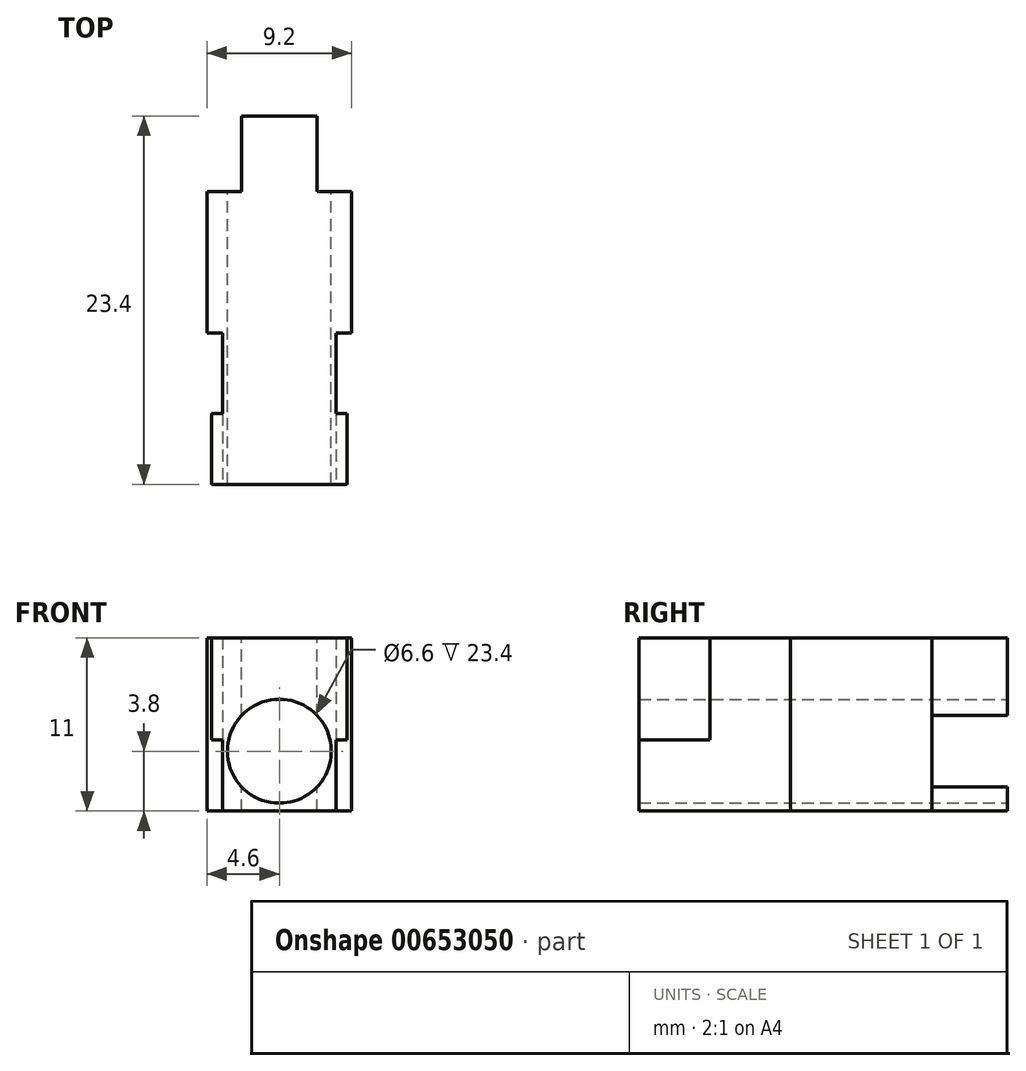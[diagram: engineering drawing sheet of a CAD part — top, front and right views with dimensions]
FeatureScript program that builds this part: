
annotation { "Feature Type Name" : "Feature", "Feature Type Description" : "" }
export const myFeature = defineFeature(function(context is Context, id is Id, definition is map)
    precondition{}
    {
        {
            var Q0;
            Q0=qCreatedBy(makeId("Front.planeOp"),FACE);
            var sketch = newSketch(context, id + "F0", { "sketchPlane" : qUnion([Q0])});
            skLineSegment(sketch, "E0.bottom", {"start": v(-3.6, 5.5) * mm, "end": v(3.6, 5.5) * mm});
            skLineSegment(sketch, "E0.top", {"start": v(-3.6, -5.5) * mm, "end": v(3.6, -5.5) * mm});
            skLineSegment(sketch, "E0.left", {"start": v(-3.6, 5.5) * mm, "end": v(-3.6, -5.5) * mm});
            skLineSegment(sketch, "E0.right", {"start": v(3.6, 5.5) * mm, "end": v(3.6, -5.5) * mm});
            skPoint(sketch, "E0.middle", {"position": v(0, 0) * mm});
            skCircle(sketch, "E1", {"center": v(0, -1.7) * mm, "radius": 3.3 * mm});
            skSolve(sketch);
        }
        {
            var Q0;
            Q0 = qSketchRegion(id + "F0", true);
            extrude(context, id + "F1", {"entities" : qUnion([Q0]), "depth" : 23.4 * mm, "offsetDistance" : 25 * mm});
        }
        {
            var Q0;
            Q0=makeQuery(id+"F1.opExtrude","SWEPT_FACE",FACE,{"disambiguationData":[OSD([sQuery(id+"F0.wireOp",EDGE,"E0.bottom")])]});
            var sketch = newSketch(context, id + "F2", { "sketchPlane" : qUnion([Q0])});
            skLineSegment(sketch, "E2.right", {"start": v(2.4, 0) * mm, "end": v(2.4, -4.8) * mm});
            skLineSegment(sketch, "E3.bottom", {"start": v(2.4, 0) * mm, "end": v(3.6, 0) * mm});
            skLineSegment(sketch, "E3.top", {"start": v(2.4, -4.8) * mm, "end": v(3.6, -4.8) * mm});
            skLineSegment(sketch, "E3.right", {"start": v(3.6, 0) * mm, "end": v(3.6, -4.8) * mm});
            skLineSegment(sketch, "E4.bottom", {"start": v(-2.4, 0) * mm, "end": v(-3.6, 0) * mm});
            skLineSegment(sketch, "E4.top", {"start": v(-2.4, -4.8) * mm, "end": v(-3.6, -4.8) * mm});
            skLineSegment(sketch, "E4.left", {"start": v(-2.4, 0) * mm, "end": v(-2.4, -4.8) * mm});
            skLineSegment(sketch, "E4.right", {"start": v(-3.6, 0) * mm, "end": v(-3.6, -4.8) * mm});
            skSolve(sketch);
        }
        {
            var Q0;
            Q0 = qSketchRegion(id + "F2", true);
            extrude(context, id + "F3", {"entities" : qUnion([Q0]), "operationType" : NewBodyOperationType.REMOVE, "endBound" : BoundingType.THROUGH_ALL, "oppositeDirection" : true, "depth" : 25 * mm, "offsetDistance" : 25 * mm});
        }
        {
            var Q0;
            Q0=makeQuery(id+"F1.opExtrude","SWEPT_FACE",FACE,{"disambiguationData":[OSD([sQuery(id+"F0.wireOp",EDGE,"E0.bottom")])]});
            var sketch = newSketch(context, id + "F4", { "sketchPlane" : qUnion([Q0])});
            skLineSegment(sketch, "E5.bottom", {"start": v(-4.6, -4.8) * mm, "end": v(4.6, -4.8) * mm});
            skLineSegment(sketch, "E5.top", {"start": v(-4.6, -13.8) * mm, "end": v(4.6, -13.8) * mm});
            skLineSegment(sketch, "E5.left", {"start": v(-4.6, -4.8) * mm, "end": v(-4.6, -13.8) * mm});
            skLineSegment(sketch, "E5.right", {"start": v(4.6, -4.8) * mm, "end": v(4.6, -13.8) * mm});
            skSolve(sketch);
        }
        {
            var Q0;
            Q0 = qSketchRegion(id + "F4", true);
            var Q1;
            Q1=makeQuery(id+"F1.opExtrude","SWEPT_FACE",FACE,{"disambiguationData":[OSD([sQuery(id+"F0.wireOp",EDGE,"E0.top")])]});
            extrude(context, id + "F5", {"entities" : qUnion([Q0]), "operationType" : NewBodyOperationType.ADD, "endBound" : BoundingType.UP_TO_SURFACE, "oppositeDirection" : true, "depth" : 25 * mm, "endBoundEntityFace" : qUnion([Q1]), "offsetDistance" : 25 * mm});
        }
        {
            var Q0;
            Q0=makeQuery(id+"F5.boolean.opBoolean","MERGE",FACE,{"derivedFrom":[makeQuery(id+"F1.opExtrude","SWEPT_FACE",FACE,{"disambiguationData":[OSD([sQuery(id+"F0.wireOp",EDGE,"E0.bottom")])]}),makeQuery(id+"F5.opExtrude","CAP_FACE",FACE,{"disambiguationData":[OSD([sQuery(id+"F4.wireOp",EDGE,"E5.bottom"),sQuery(id+"F4.wireOp",EDGE,"E5.top"),sQuery(id+"F4.wireOp",EDGE,"E5.left"),sQuery(id+"F4.wireOp",EDGE,"E5.right")])],"isStart":true})]});
            var sketch = newSketch(context, id + "F6", { "sketchPlane" : qUnion([Q0])});
            skLineSegment(sketch, "E6.bottom", {"start": v(-4.3, -23.4) * mm, "end": v(4.3, -23.4) * mm});
            skLineSegment(sketch, "E6.top", {"start": v(-4.3, -18.9) * mm, "end": v(4.3, -18.9) * mm});
            skLineSegment(sketch, "E6.left", {"start": v(-4.3, -23.4) * mm, "end": v(-4.3, -18.9) * mm});
            skLineSegment(sketch, "E6.right", {"start": v(4.3, -23.4) * mm, "end": v(4.3, -18.9) * mm});
            skSolve(sketch);
        }
        {
            var Q0;
            Q0 = qSketchRegion(id + "F6", true);
            var Q1;
            {var subQ0=sQuery(id+"F0.wireOp",EDGE,"E0.top");Q1=makeQuery(id+"F5.boolean.opBoolean","MERGE",FACE,{"derivedFrom":[makeQuery(id+"F1.opExtrude","SWEPT_FACE",FACE,{"disambiguationData":[OSD([subQ0])]}),makeQuery(id+"F5.opExtrude","CAP_FACE",FACE,{"disambiguationData":[OSD([subQ0])],"isStart":false})]});}
            extrude(context, id + "F7", {"entities" : qUnion([Q0]), "operationType" : NewBodyOperationType.ADD, "oppositeDirection" : true, "depth" : 6.5 * mm, "endBoundEntityFace" : qUnion([Q1]), "offsetDistance" : 25 * mm});
        }
        {
            var Q0;
            Q0=makeQuery(id+"F7.boolean.opBoolean","MERGE",FACE,{"derivedFrom":[makeQuery(id+"F1.opExtrude","CAP_FACE",FACE,{"disambiguationData":[OSD([sQuery(id+"F0.wireOp",EDGE,"E0.bottom"),sQuery(id+"F0.wireOp",EDGE,"E0.top"),sQuery(id+"F0.wireOp",EDGE,"E0.left"),sQuery(id+"F0.wireOp",EDGE,"E0.right"),sQuery(id+"F0.wireOp",EDGE,"E1")])],"isStart":false}),makeQuery(id+"F7.opExtrude","SWEPT_FACE",FACE,{"disambiguationData":[OSD([sQuery(id+"F6.wireOp",EDGE,"E6.bottom")])]})]});
            var sketch = newSketch(context, id + "F8", { "sketchPlane" : qUnion([Q0])});
            skCircle(sketch, "E7", {"center": v(0, -1.7) * mm, "radius": 3.3 * mm});
            skSolve(sketch);
        }
        {
            var Q0;
            Q0 = qSketchRegion(id + "F8", true);
            extrude(context, id + "F9", {"entities" : qUnion([Q0]), "operationType" : NewBodyOperationType.REMOVE, "endBound" : BoundingType.THROUGH_ALL, "oppositeDirection" : true, "depth" : 25 * mm, "offsetDistance" : 25 * mm});
        }
    });
